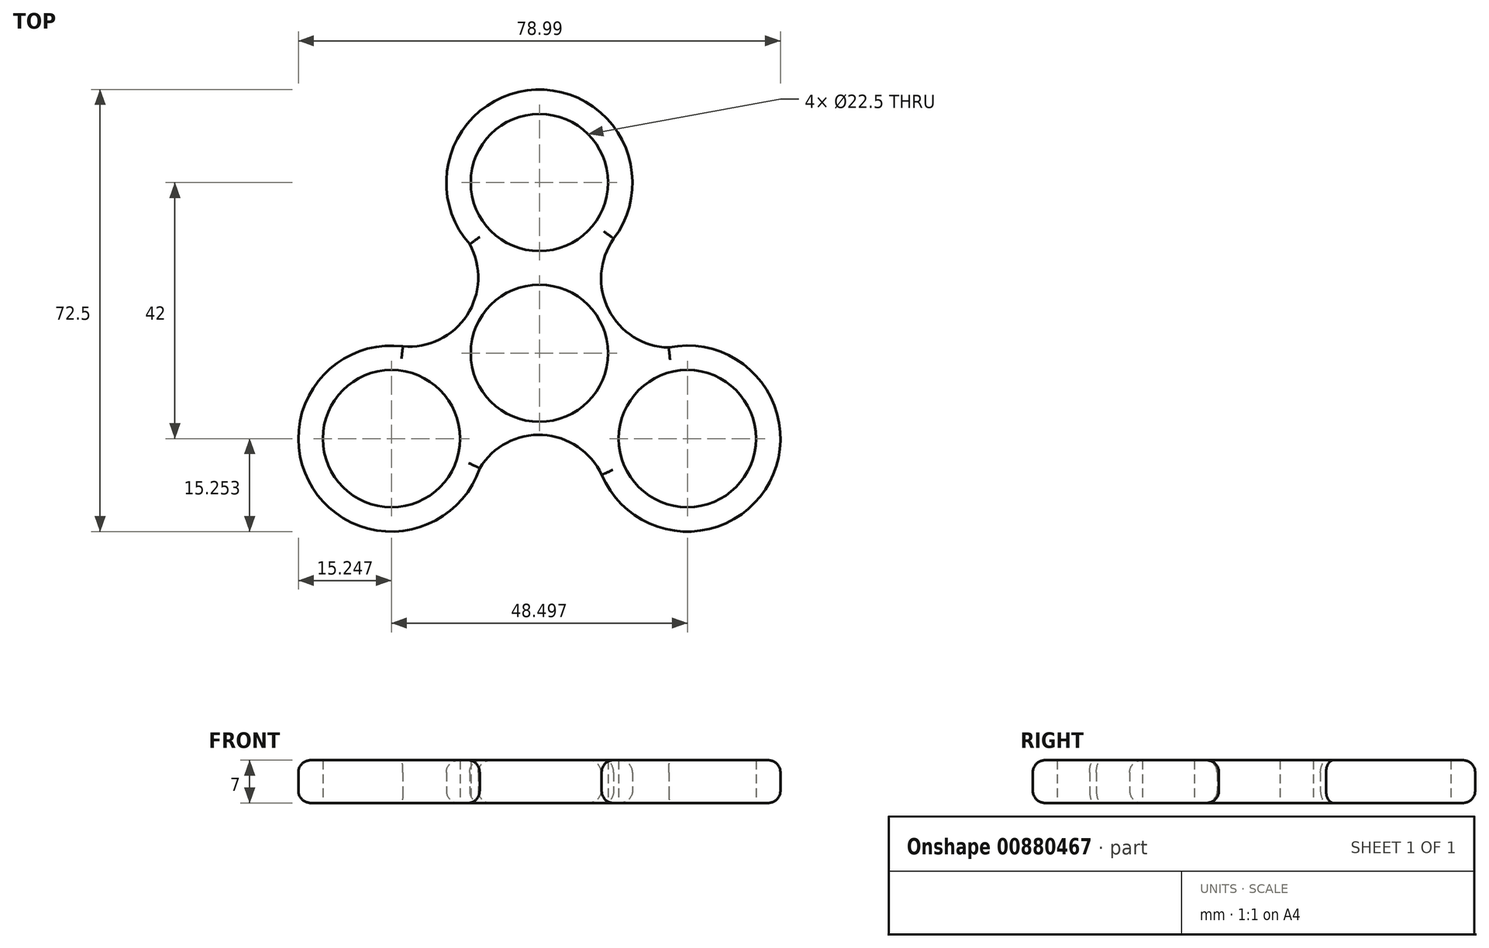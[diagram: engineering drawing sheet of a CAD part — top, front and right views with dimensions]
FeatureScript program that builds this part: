
annotation { "Feature Type Name" : "Feature", "Feature Type Description" : "" }
export const myFeature = defineFeature(function(context is Context, id is Id, definition is map)
    precondition{}
    {
        {
            var Q0;
            Q0=qCreatedBy(makeId("Top.planeOp"),FACE);
            var sketch = newSketch(context, id + "F0", { "sketchPlane" : qUnion([Q0])});
            skCircle(sketch, "E0", {"center": v(-7.06, 1.64) * mm, "radius": 11.25 * mm});
            skCircle(sketch, "E1", {"center": v(-7.06, 29.64) * mm, "radius": 11.25 * mm});
            skCircle(sketch, "E2.1.0", {"center": v(-31.31, -12.36) * mm, "radius": 11.25 * mm});
            skCircle(sketch, "E2.2.0", {"center": v(17.18, -12.36) * mm, "radius": 11.25 * mm});
            skCircle(sketch, "E3.0", {"center": v(-7.06, 29.64) * mm, "radius": 15.25 * mm});
            skCircle(sketch, "E4.0", {"center": v(-31.31, -12.36) * mm, "radius": 15.25 * mm});
            skCircle(sketch, "E5.0", {"center": v(17.18, -12.36) * mm, "radius": 15.25 * mm});
            skArc(sketch, "E6", {"start": v(-29.44, 2.78) * mm, "mid": v(-18.94, 7.88) * mm, "end": v(-18.49, 19.54) * mm});
            skArc(sketch, "E7.1.0", {"start": v(3.14, -18.3) * mm, "mid": v(-6.52, -11.76) * mm, "end": v(-16.85, -17.2) * mm});
            skArc(sketch, "E7.2.0", {"start": v(5.1, 20.45) * mm, "mid": v(4.27, 8.81) * mm, "end": v(14.14, 2.59) * mm});
            skSolve(sketch);
        }
        {
            var Q0;
            Q0=makeQuery(id+"F0.imprint","IMPRINT",FACE,{"disambiguationData":[TD([[makeQuery(id+"F0.imprint","IMPRINT",EDGE,{"derivedFrom":sQuery(id+"F0.wireOp",EDGE,"E2.1.0")}),-1.0]])]});
            var Q1;
            Q1=makeQuery(id+"F0.imprint","IMPRINT",FACE,{"disambiguationData":[TD([[makeQuery(id+"F0.imprint","IMPRINT",EDGE,{"derivedFrom":sQuery(id+"F0.wireOp",EDGE,"E2.2.0")}),-1.0]])]});
            var Q2;
            Q2=makeQuery(id+"F0.imprint","IMPRINT",FACE,{"disambiguationData":[TD([[makeQuery(id+"F0.imprint","IMPRINT",EDGE,{"derivedFrom":sQuery(id+"F0.wireOp",EDGE,"E0")}),-1.0]])]});
            var Q3;
            Q3=makeQuery(id+"F0.imprint","IMPRINT",FACE,{"disambiguationData":[TD([[makeQuery(id+"F0.imprint","IMPRINT",EDGE,{"derivedFrom":sQuery(id+"F0.wireOp",EDGE,"E1")}),-1.0]])]});
            extrude(context, id + "F1", {"entities" : qUnion([Q0, Q1, Q2, Q3]), "depth" : 7 * mm, "offsetDistance" : 25 * mm});
        }
        {
            var Q0;
            Q0=makeQuery(id+"F1.opExtrude","CAP_EDGE",EDGE,{"disambiguationData":[OSD([sQuery(id+"F0.wireOp",EDGE,"E3.0")])],"isStart":false});
            var Q1;
            Q1=makeQuery(id+"F1.opExtrude","CAP_EDGE",EDGE,{"disambiguationData":[OSD([sQuery(id+"F0.wireOp",EDGE,"E7.2.0")])],"isStart":false});
            var Q2;
            Q2=makeQuery(id+"F1.opExtrude","CAP_EDGE",EDGE,{"disambiguationData":[OSD([sQuery(id+"F0.wireOp",EDGE,"E5.0")])],"isStart":false});
            var Q3;
            Q3=makeQuery(id+"F1.opExtrude","CAP_EDGE",EDGE,{"disambiguationData":[OSD([sQuery(id+"F0.wireOp",EDGE,"E6")])],"isStart":false});
            var Q4;
            Q4=makeQuery(id+"F1.opExtrude","CAP_EDGE",EDGE,{"disambiguationData":[OSD([sQuery(id+"F0.wireOp",EDGE,"E4.0")])],"isStart":false});
            var Q5;
            Q5=makeQuery(id+"F1.opExtrude","CAP_EDGE",EDGE,{"disambiguationData":[OSD([sQuery(id+"F0.wireOp",EDGE,"E6")])],"isStart":true});
            var Q6;
            Q6=makeQuery(id+"F1.opExtrude","CAP_EDGE",EDGE,{"disambiguationData":[OSD([sQuery(id+"F0.wireOp",EDGE,"E3.0")])],"isStart":true});
            var Q7;
            Q7=makeQuery(id+"F1.opExtrude","CAP_EDGE",EDGE,{"disambiguationData":[OSD([sQuery(id+"F0.wireOp",EDGE,"E4.0")])],"isStart":true});
            var Q8;
            Q8=makeQuery(id+"F1.opExtrude","CAP_EDGE",EDGE,{"disambiguationData":[OSD([sQuery(id+"F0.wireOp",EDGE,"E7.1.0")])],"isStart":true});
            var Q9;
            Q9=makeQuery(id+"F1.opExtrude","CAP_EDGE",EDGE,{"disambiguationData":[OSD([sQuery(id+"F0.wireOp",EDGE,"E5.0")])],"isStart":true});
            fillet(context, id + "F2", {"entities" : qUnion([Q0, Q1, Q2, Q3, Q4, Q5, Q6, Q7, Q8, Q9]), "radius" : 2 * mm, "tangentPropagation" : true, "allowEdgeOverflow" : false});
        }
    });
